# Revit family: AV5080001_Grifería Lavaplatos 8 pulgadas Aluvia Triceta
name_source: partatom
category: Plumbing Fixtures
units: mm (PartAtom-declared; Revit-internal decimal feet)

## family parameters
Cut with Voids When Loaded = No
Host = Face
OmniClass Number = 23.31.11.00
Part Type = Normal
Room Calculation Point = No
Round Connector Dimension = Use Diameter
Shared = No

## types (1)
- AV5080001_Grifería Lavaplatos 8 pulgadas Aluvia Triceta
    Alto = 336 mm  [stored 1.10236 ft]
    Ancho = 260 mm  [stored 0.853018 ft]
    Creado por = BIMBAU
    Default Elevation = 1219 mm
    Description = La grifería de cocina Aluvia ha sido diseñada para trabajar en perfecta armonía con el espacio. Su pico giratorio le permite al usuario tomar ventaja de toda el área de la poceta. Pico alto que permite el lavado de elementos de gran tamaño, dando confortnen el uso.
    Fecha de creación = 10/03/2021
    Garantía = 30  Años Grival - 2 Años Cromado
    Manufacturer = Corona
    Material = Corona_Aluminio
    Model = Griferia LavaPlatos Aluvia 8 Pulgadas Triceta
    Presion maxima = 125 psi (862 Kpa).
    Presion minima = 20 psi (138 Kpa).
    Profundidad = 198 mm  [stored 0.649606 ft]
    Referencia = AV5060001
    SKU = AV5060001
    Vida Util (Giratorio) = 50.000 ciclos.
    Vida útil = 500.000 ciclos.

note: [stored X ft] marks values corroborated as IEEE doubles in the binary element streams (Revit-internal decimal feet)

## geometry (parser evidence)
native form markers: Blend x2, Sweep x5
no freeform markers — native parametric forms only
